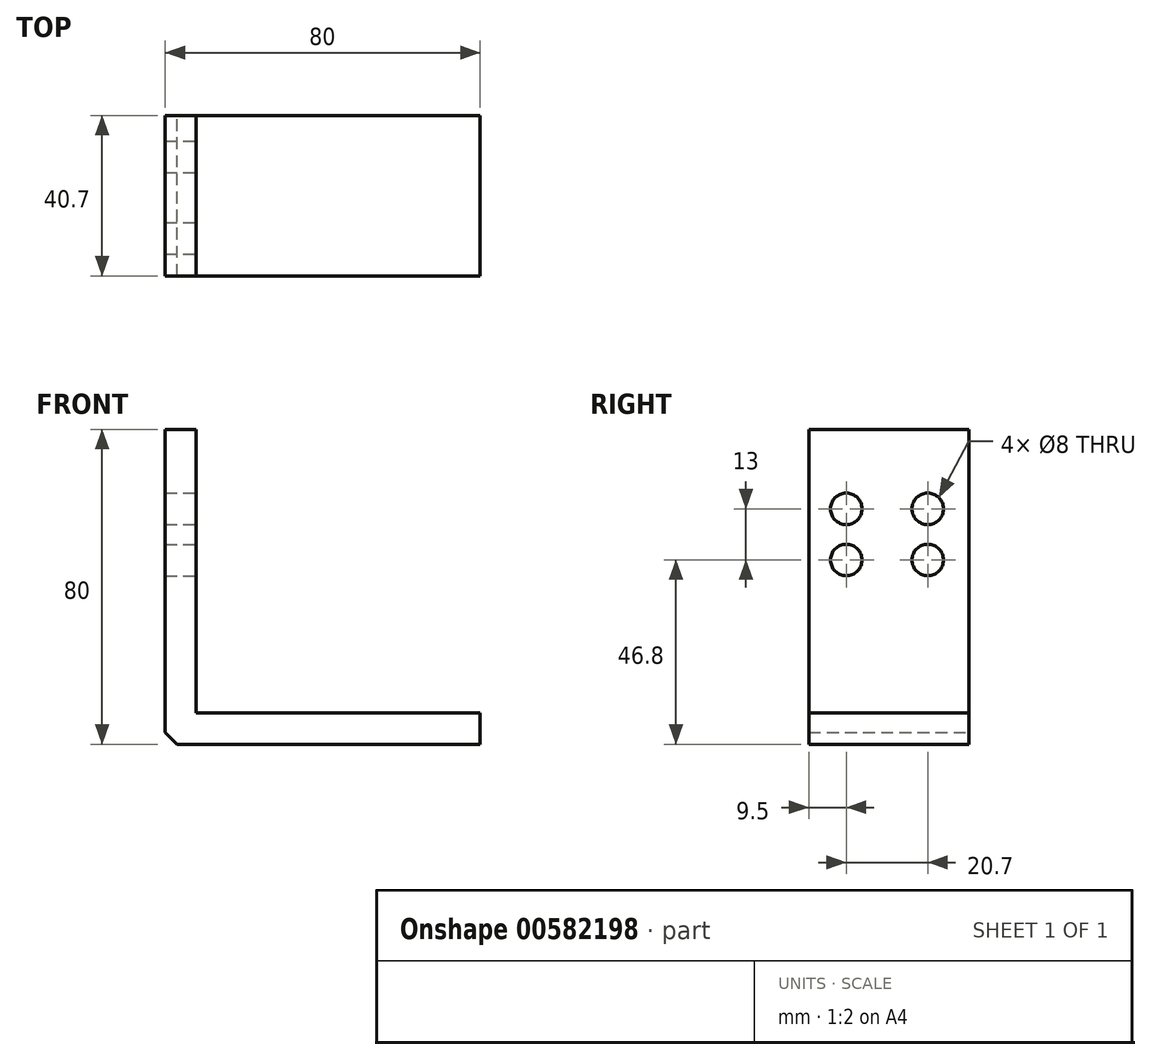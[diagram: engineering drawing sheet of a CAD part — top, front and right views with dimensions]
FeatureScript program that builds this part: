
annotation { "Feature Type Name" : "Feature", "Feature Type Description" : "" }
export const myFeature = defineFeature(function(context is Context, id is Id, definition is map)
    precondition{}
    {
        {
            var Q0;
            Q0=qCreatedBy(makeId("Front.planeOp"),FACE);
            var sketch = newSketch(context, id + "F0", { "sketchPlane" : qUnion([Q0])});
            skLineSegment(sketch, "E0", {"start": v(0, 80) * mm, "end": v(0, 3) * mm});
            skLineSegment(sketch, "E1", {"start": v(3, 0) * mm, "end": v(80, 0) * mm});
            skLineSegment(sketch, "E2", {"start": v(80, 0) * mm, "end": v(80, 7.9) * mm});
            skLineSegment(sketch, "E3", {"start": v(80, 7.9) * mm, "end": v(7.9, 7.9) * mm});
            skLineSegment(sketch, "E4", {"start": v(7.9, 7.9) * mm, "end": v(7.9, 80) * mm});
            skLineSegment(sketch, "E5", {"start": v(7.9, 80) * mm, "end": v(0, 80) * mm});
            skLineSegment(sketch, "E6", {"start": v(3, 0) * mm, "end": v(0, 3) * mm});
            skPoint(sketch, "E7.orphan", {"position": v(0, 0) * mm});
            skSolve(sketch);
        }
        {
            var Q0;
            Q0 = qSketchRegion(id + "F0", true);
            extrude(context, id + "F1", {"entities" : qUnion([Q0]), "depth" : 40.7 * mm, "offsetDistance" : 25 * mm});
        }
        {
            var Q0;
            Q0=makeQuery(id+"F1.opExtrude","SWEPT_FACE",FACE,{"disambiguationData":[OSD([sQuery(id+"F0.wireOp",EDGE,"E4")])]});
            var sketch = newSketch(context, id + "F2", { "sketchPlane" : qUnion([Q0])});
            skCircle(sketch, "E8", {"center": v(-31.2, 59.8) * mm, "radius": 4 * mm});
            skCircle(sketch, "E9", {"center": v(-31.2, 46.8) * mm, "radius": 4 * mm});
            skCircle(sketch, "E10", {"center": v(-10.5, 46.8) * mm, "radius": 4 * mm});
            skCircle(sketch, "E11", {"center": v(-10.5, 59.8) * mm, "radius": 4 * mm});
            skSolve(sketch);
        }
        {
            var Q0;
            Q0 = qSketchRegion(id + "F2", true);
            extrude(context, id + "F3", {"entities" : qUnion([Q0]), "operationType" : NewBodyOperationType.REMOVE, "oppositeDirection" : true, "depth" : 25 * mm, "offsetDistance" : 25 * mm});
        }
    });
